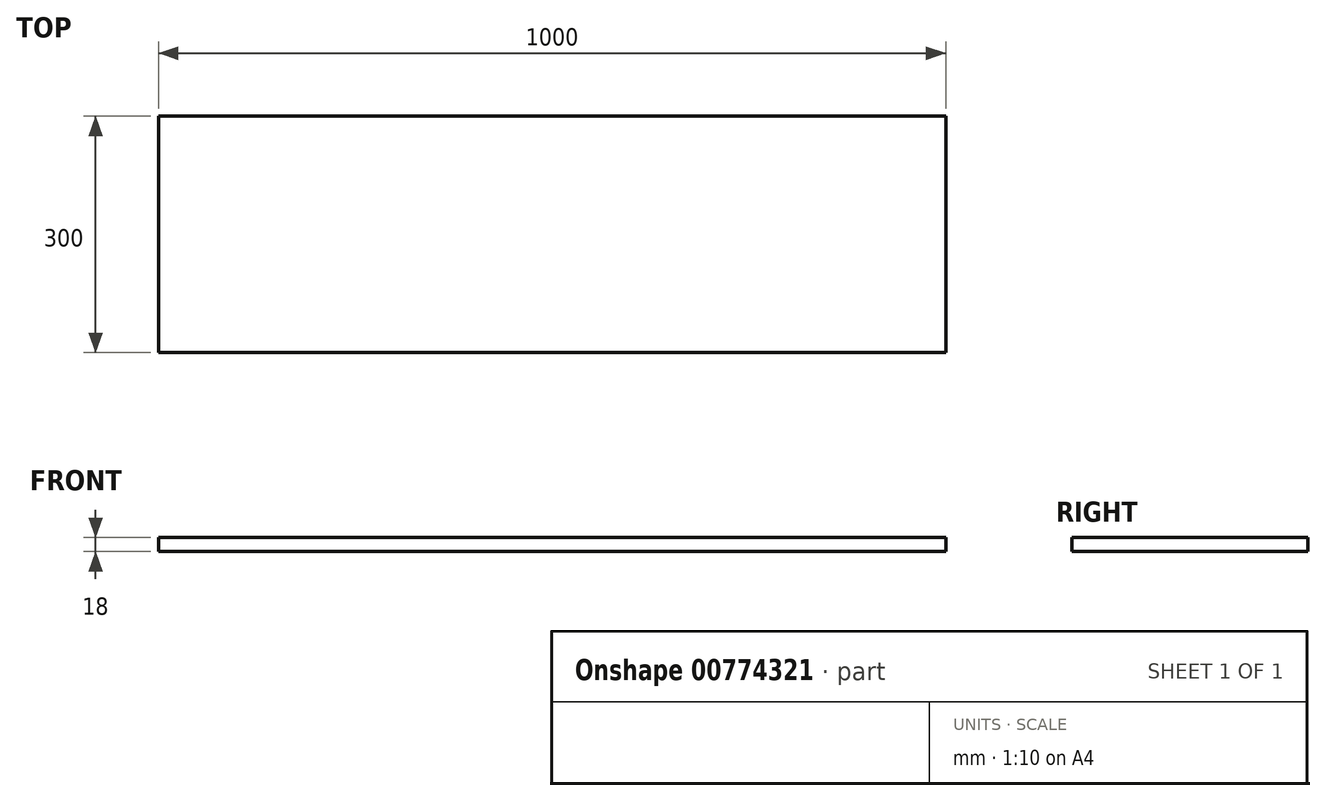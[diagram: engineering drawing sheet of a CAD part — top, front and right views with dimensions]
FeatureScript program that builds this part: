
annotation { "Feature Type Name" : "Feature", "Feature Type Description" : "" }
export const myFeature = defineFeature(function(context is Context, id is Id, definition is map)
    precondition{}
    {
        {
            var Q0;
            Q0=qCreatedBy(makeId("Top.planeOp"),FACE);
            var sketch = newSketch(context, id + "F0", { "sketchPlane" : qUnion([Q0])});
            skLineSegment(sketch, "E0.bottom", {"start": v(500, 150) * mm, "end": v(-500, 150) * mm});
            skLineSegment(sketch, "E0.top", {"start": v(500, -150) * mm, "end": v(-500, -150) * mm});
            skLineSegment(sketch, "E0.right", {"start": v(-500, 150) * mm, "end": v(-500, -150) * mm});
            skPoint(sketch, "E0.middle", {"position": v(0, 0) * mm});
            skLineSegment(sketch, "E1", {"start": v(500, 150) * mm, "end": v(500, -150) * mm});
            skSolve(sketch);
        }
        {
            var Q0;
            Q0=makeQuery(id+"F0.imprint","IMPRINT",FACE,{"disambiguationData":[TD([[makeQuery(id+"F0.imprint","IMPRINT",EDGE,{"derivedFrom":sQuery(id+"F0.wireOp",EDGE,"E0.bottom")}),1.0]])]});
            extrude(context, id + "F1", {"entities" : qUnion([Q0]), "depth" : 18 * mm, "offsetDistance" : 25 * mm});
        }
    });
